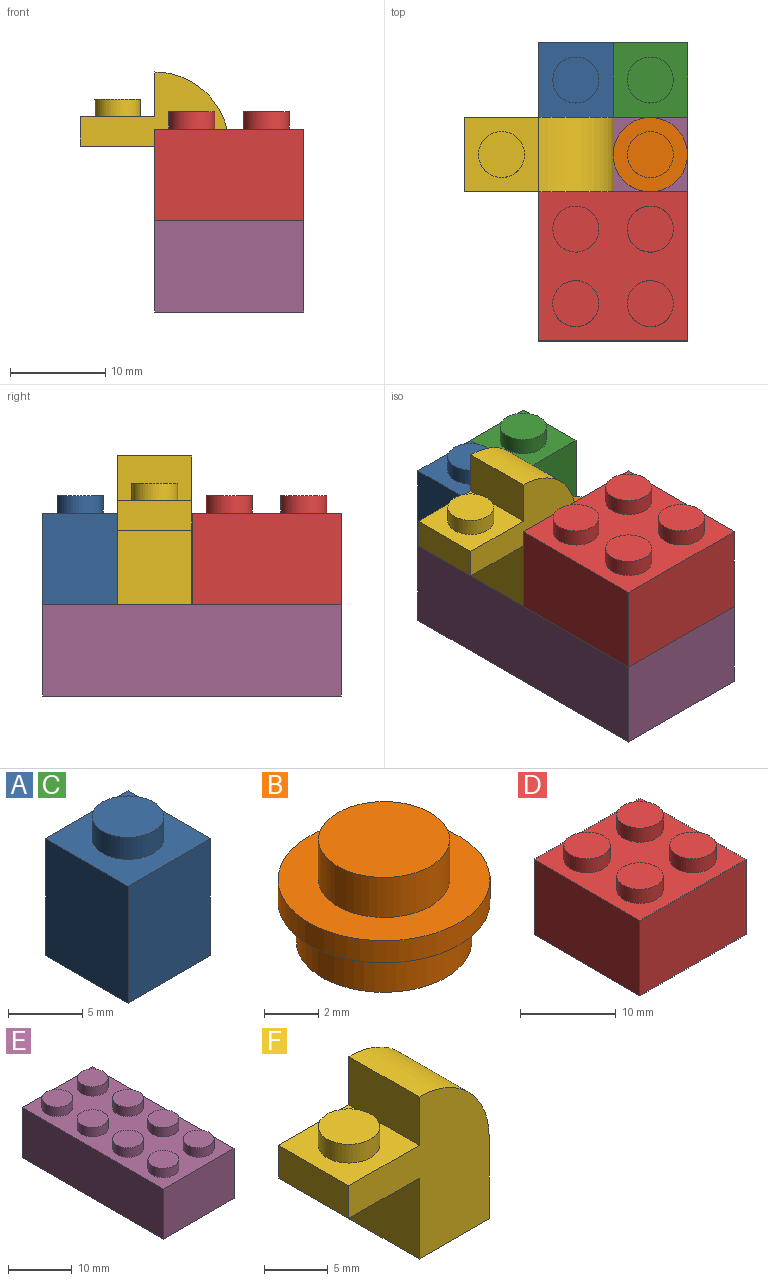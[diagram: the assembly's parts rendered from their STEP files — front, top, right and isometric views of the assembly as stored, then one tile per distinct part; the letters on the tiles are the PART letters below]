
ASSEMBLY  parts=6 mates=5
PART A: 13 faces, bbox 7.8x7.8x11.4 mm
  f0: plane 7.83x7.83mm, normal (0,0,-1), area 38mm2, adj f2,f3,f4,f5,f8,f9,f10,f11
  f1: plane 7.83x7.83mm, normal (0,0,1), area 43mm2, adj f2,f3,f4,f5,f6
  f2: plane 9.61x7.83mm, normal (-1,0,0), area 75.2mm2, adj f0,f1,f4,f5
  f3: plane 9.61x7.83mm, normal (1,0,0), area 75.2mm2, adj f0,f1,f4,f5
  f4: plane 9.61x7.83mm, normal (0,-1,0), area 75.2mm2, adj f0,f1,f2,f3
  f5: plane 9.61x7.83mm, normal (0,1,0), area 75.2mm2, adj f0,f1,f2,f3
  f6: cylinder r=2.42mm len=4.83mm, axis (0,0,-1), area 27.3mm2, adj f1,f7
  f7: plane 4.83x4.83mm, normal (0,0,1), area 18.3mm2, adj f6
  f8: plane 8.11x4.83mm, normal (0,1,0), area 39.2mm2, adj f0,f9,f11,f12
  f9: plane 8.11x4.83mm, normal (1,0,0), area 39.2mm2, adj f0,f8,f10,f12
  f10: plane 8.11x4.83mm, normal (0,-1,0), area 39.2mm2, adj f0,f9,f11,f12
  f11: plane 8.11x4.83mm, normal (-1,0,0), area 39.2mm2, adj f0,f8,f10,f12
  f12: plane 4.83x4.83mm, normal (0,0,-1), area 23.3mm2, adj f8,f9,f10,f11
PART B: 9 faces, bbox 7.8x7.8x4.6 mm
  f0: cylinder r=2.43mm len=4.85mm, axis (0,0,1), area 27.4mm2, adj f1,f8
  f1: plane 4.85x4.85mm, normal (0,0,-1), area 18.5mm2, adj f0
  f2: plane 4.83x4.83mm, normal (0,0,1), area 18.3mm2, adj f3
  f3: cylinder r=2.42mm len=4.83mm, axis (0,0,1), area 27.3mm2, adj f2,f4
  f4: plane 7.8x7.8mm, normal (0,0,1), area 29.5mm2, adj f3,f5
  f5: cylinder r=3.9mm len=7.8mm, axis (0,0,1), area 24.5mm2, adj f4,f6
  f6: plane 7.8x7.8mm, normal (0,0,-1), area 15.1mm2, adj f5,f7
  f7: cylinder r=3.23mm len=6.45mm, axis (0,0,1), area 36.5mm2, adj f6,f8
  f8: plane 6.45x6.45mm, normal (0,0,-1), area 14.2mm2, adj f0,f7
PART C: same geometry as A
PART D: 30 faces, bbox 15.7x15.7x11.4 mm
  f0: plane 13.26x6.23mm, normal (0,0,-1), area 71.7mm2, adj f2,f18,f19,f21,f24,f27
  f1: plane 13.26x6.23mm, normal (0,0,-1), area 71.7mm2, adj f2,f17,f19,f20,f23,f27
  f2: plane 13.26x8.11mm, normal (1,0,0), area 102.2mm2, adj f0,f1,f3,f17,f18,f23,f24,f25
  f3: plane 15.66x15.66mm, normal (0,0,-1), area 69.4mm2, adj f2,f4,f6,f7,f8,f17,f18,f19
  f4: plane 15.66x9.61mm, normal (1,0,0), area 150.5mm2, adj f3,f5,f7,f8
  f5: plane 15.66x15.66mm, normal (0,0,1), area 171.9mm2, adj f4,f6,f7,f8,f9,f11,f13,f15
  f6: plane 15.66x9.61mm, normal (-1,0,0), area 150.5mm2, adj f3,f5,f7,f8
  f7: plane 15.66x9.61mm, normal (0,-1,0), area 150.5mm2, adj f3,f4,f5,f6
  f8: plane 15.66x9.61mm, normal (0,1,0), area 150.5mm2, adj f3,f4,f5,f6
  f9: cylinder r=2.42mm len=4.83mm, axis (0,0,-1), area 27.3mm2, adj f5,f10
  f10: plane 4.83x4.83mm, normal (0,0,1), area 18.3mm2, adj f9
  f11: cylinder r=2.42mm len=4.83mm, axis (0,0,-1), area 27.3mm2, adj f5,f12
  f12: plane 4.83x4.83mm, normal (0,0,1), area 18.3mm2, adj f11
  f13: cylinder r=2.42mm len=4.83mm, axis (0,0,-1), area 27.3mm2, adj f5,f14
  f14: plane 4.83x4.83mm, normal (0,0,1), area 18.3mm2, adj f13
  f15: cylinder r=2.42mm len=4.83mm, axis (0,0,-1), area 27.3mm2, adj f5,f16
  f16: plane 4.83x4.83mm, normal (0,0,1), area 18.3mm2, adj f15
  f17: plane 13.26x8.11mm, normal (0,1,0), area 107.5mm2, adj f1,f2,f3,f19
  f18: plane 13.26x8.11mm, normal (0,-1,0), area 107.5mm2, adj f0,f2,f3,f19
  f19: plane 13.26x8.11mm, normal (-1,0,0), area 102.2mm2, adj f0,f1,f3,f17,f18,f20,f21,f22
  f20: plane 6.61x3.76mm, normal (0,-1,0), area 24.8mm2, adj f1,f19,f22,f27
  f21: plane 6.61x3.76mm, normal (0,1,0), area 24.8mm2, adj f0,f19,f22,f27
  f22: plane 3.76x0.81mm, normal (0,0,-1), area 3mm2, adj f19,f20,f21,f27
  f23: plane 6.61x3.76mm, normal (0,-1,0), area 24.8mm2, adj f1,f2,f25,f27
  f24: plane 6.61x3.76mm, normal (0,1,0), area 24.8mm2, adj f0,f2,f25,f27
  f25: plane 3.76x0.81mm, normal (0,0,-1), area 3mm2, adj f2,f23,f24,f27
  f26: cylinder r=2.5mm len=8.11mm, axis (0,0,1), area 127.4mm2, adj f28,f29
  f27: cylinder r=2.9mm len=8.11mm, axis (0,0,1), area 137mm2, adj f0,f1,f20,f21,f22,f23,f24,f25
  f28: plane 5.8x5.8mm, normal (0,0,-1), area 6.8mm2, adj f26,f27
  f29: plane 5x5mm, normal (0,0,-1), area 19.6mm2, adj f26
PART E: 46 faces, bbox 15.7x31.3x11.4 mm
  f0: plane 14.06x13.26mm, normal (0,0,-1), area 149.1mm2, adj f2,f26,f27,f29,f32,f35,f39
  f1: plane 14.06x13.26mm, normal (0,0,-1), area 149.1mm2, adj f2,f25,f27,f28,f31,f35,f43
  f2: plane 28.92x8.11mm, normal (1,0,0), area 229.2mm2, adj f0,f1,f3,f25,f26,f28,f29,f30
  f3: plane 31.32x15.66mm, normal (0,0,-1), area 107mm2, adj f2,f4,f6,f7,f8,f25,f26,f27
  f4: plane 31.32x9.61mm, normal (1,0,0), area 301mm2, adj f3,f5,f7,f8
  f5: plane 31.32x15.66mm, normal (0,0,1), area 343.9mm2, adj f4,f6,f7,f8,f9,f11,f13,f15
  f6: plane 31.32x9.61mm, normal (-1,0,0), area 301mm2, adj f3,f5,f7,f8
  f7: plane 15.66x9.61mm, normal (0,-1,0), area 150.5mm2, adj f3,f4,f5,f6
  f8: plane 15.66x9.61mm, normal (0,1,0), area 150.5mm2, adj f3,f4,f5,f6
  f9: cylinder r=2.42mm len=4.83mm, axis (0,0,-1), area 27.3mm2, adj f5,f10
  f10: plane 4.83x4.83mm, normal (0,0,1), area 18.3mm2, adj f9
  f11: cylinder r=2.42mm len=4.83mm, axis (0,0,-1), area 27.3mm2, adj f5,f12
  f12: plane 4.83x4.83mm, normal (0,0,1), area 18.3mm2, adj f11
  f13: cylinder r=2.42mm len=4.83mm, axis (0,0,-1), area 27.3mm2, adj f5,f14
  f14: plane 4.83x4.83mm, normal (0,0,1), area 18.3mm2, adj f13
  f15: cylinder r=2.42mm len=4.83mm, axis (0,0,-1), area 27.3mm2, adj f5,f16
  f16: plane 4.83x4.83mm, normal (0,0,1), area 18.3mm2, adj f15
  f17: cylinder r=2.42mm len=4.83mm, axis (0,0,-1), area 27.3mm2, adj f5,f18
  f18: plane 4.83x4.83mm, normal (0,0,1), area 18.3mm2, adj f17
  f19: cylinder r=2.42mm len=4.83mm, axis (0,0,-1), area 27.3mm2, adj f5,f20
  f20: plane 4.83x4.83mm, normal (0,0,1), area 18.3mm2, adj f19
  f21: cylinder r=2.42mm len=4.83mm, axis (0,0,-1), area 27.3mm2, adj f5,f22
  f22: plane 4.83x4.83mm, normal (0,0,1), area 18.3mm2, adj f21
  f23: cylinder r=2.42mm len=4.83mm, axis (0,0,-1), area 27.3mm2, adj f5,f24
  f24: plane 4.83x4.83mm, normal (0,0,1), area 18.3mm2, adj f23
  f25: plane 13.26x8.11mm, normal (0,1,0), area 107.5mm2, adj f1,f2,f3,f27
  f26: plane 13.26x8.11mm, normal (0,-1,0), area 107.5mm2, adj f0,f2,f3,f27
  f27: plane 28.92x8.11mm, normal (-1,0,0), area 229.2mm2, adj f0,f1,f3,f25,f26,f31,f32,f33
  f28: plane 6.61x3.76mm, normal (0,-1,0), area 24.8mm2, adj f1,f2,f30,f35
  f29: plane 6.61x3.76mm, normal (0,1,0), area 24.8mm2, adj f0,f2,f30,f35
  f30: plane 3.76x0.81mm, normal (0,0,-1), area 3mm2, adj f2,f28,f29,f35
  f31: plane 6.61x3.76mm, normal (0,-1,0), area 24.8mm2, adj f1,f27,f33,f35
  f32: plane 6.61x3.76mm, normal (0,1,0), area 24.8mm2, adj f0,f27,f33,f35
  f33: plane 3.76x0.81mm, normal (0,0,-1), area 3mm2, adj f27,f31,f32,f35
  f34: cylinder r=2.5mm len=8.11mm, axis (0,0,1), area 127.4mm2, adj f36,f37
  f35: cylinder r=2.9mm len=8.11mm, axis (0,0,1), area 137mm2, adj f0,f1,f28,f29,f30,f31,f32,f33
  f36: plane 5.8x5.8mm, normal (0,0,-1), area 6.8mm2, adj f34,f35
  f37: plane 5x5mm, normal (0,0,-1), area 19.6mm2, adj f34
  f38: cylinder r=2.5mm len=8.11mm, axis (0,0,1), area 127.4mm2, adj f40,f41
  f39: cylinder r=2.9mm len=8.11mm, axis (0,0,1), area 147.8mm2, adj f0,f40
  f40: plane 5.8x5.8mm, normal (0,0,-1), area 6.8mm2, adj f38,f39
  f41: plane 5x5mm, normal (0,0,-1), area 19.6mm2, adj f38
  f42: cylinder r=2.5mm len=8.11mm, axis (0,0,1), area 127.4mm2, adj f44,f45
  f43: cylinder r=2.9mm len=8.11mm, axis (0,0,1), area 147.8mm2, adj f1,f44
  f44: plane 5.8x5.8mm, normal (0,0,-1), area 6.8mm2, adj f42,f43
  f45: plane 5x5mm, normal (0,0,-1), area 19.6mm2, adj f42
PART F: 22 faces, bbox 15.6x7.8x15.6 mm
  f0: plane 7.8x7.8mm, normal (0,0,-1), area 30.6mm2, adj f3,f5,f6,f8,f18,f19,f20
  f1: plane 7.8x7.8mm, normal (0,0,-1), area 37.8mm2, adj f3,f4,f5,f6,f12,f13,f14,f15
  f2: plane 7.8x4.65mm, normal (-1,0,0), area 36.3mm2, adj f3,f5,f7,f9
  f3: plane 15.6x15.6mm, normal (0,-1,0), area 133.2mm2, adj f0,f1,f2,f4,f6,f7,f8,f9
  f4: plane 7.8x7.8mm, normal (1,0,0), area 60.8mm2, adj f1,f3,f5,f7
  f5: plane 15.6x15.6mm, normal (0,1,0), area 133.2mm2, adj f0,f1,f2,f4,f6,f7,f8,f9
  f6: plane 9.45x7.8mm, normal (-1,0,0), area 68.8mm2, adj f0,f1,f3,f5,f18,f20,f21
  f7: cylinder r=7.8mm len=7.8mm, axis (0,1,0), area 95.6mm2, adj f2,f3,f4,f5
  f8: plane 7.8x3.15mm, normal (-1,0,0), area 24.6mm2, adj f0,f3,f5,f9
  f9: plane 7.8x7.8mm, normal (0,0,1), area 42.5mm2, adj f2,f3,f5,f8,f10
  f10: cylinder r=2.42mm len=4.83mm, axis (0,0,-1), area 27.3mm2, adj f9,f11
  f11: plane 4.83x4.83mm, normal (0,0,1), area 18.3mm2, adj f10
  f12: plane 13.95x4.83mm, normal (0,1,0), area 59.5mm2, adj f1,f13,f15,f16,f17
  f13: plane 13.95x4.8mm, normal (1,0,0), area 67mm2, adj f1,f12,f14,f16
  f14: plane 13.95x4.83mm, normal (0,-1,0), area 59.5mm2, adj f1,f13,f15,f16,f17
  f15: plane 7.79x4.8mm, normal (-1,0,0), area 37.4mm2, adj f1,f12,f14,f17
  f16: cylinder r=6.33mm len=6.17mm, axis (0,-1,0), area 40.6mm2, adj f12,f13,f14,f17
  f17: plane 4.8x0.03mm, normal (0,0,1), area 0.2mm2, adj f12,f14,f15,f16
  f18: plane 6.3x1.65mm, normal (0,-1,0), area 10.4mm2, adj f0,f6,f19,f21
  f19: plane 4.8x1.65mm, normal (1,0,0), area 7.9mm2, adj f0,f18,f20,f21
  f20: plane 6.3x1.65mm, normal (0,1,0), area 10.4mm2, adj f0,f6,f19,f21
  f21: plane 6.3x4.8mm, normal (0,0,-1), area 30.2mm2, adj f6,f18,f19,f20
PLACE A t=(-20.55,-0.29,-4.38)mm
PLACE B t=(-12.72,-12.03,-6.89)mm
PLACE C t=(-12.72,-0.29,-4.38)mm
PLACE D t=(-16.63,-15.95,-4.38)mm
PLACE E t=(-16.63,-0.29,-13.99)mm
PLACE F t=(-20.55,-12.03,-9.19)mm
MATE fastened B.f0 <-> E.f19  axis (0,0,-1) through (-12.72,-12.03,-9.19)mm
MATE fastened F.f1 <-> E.f17  axis (0,0,-1) through (-20.55,-12.03,-9.19)mm
MATE fastened D.f3 <-> E.f5  axis (0,0,-1) through (-24.46,-31.61,-9.19)mm
MATE fastened E.f23 <-> C.f6  axis (0,0,-1) through (-12.72,-4.2,-9.19)mm
MATE fastened E.f21 <-> A.f6  axis (0,0,-1) through (-20.55,-4.2,-9.19)mm
